FCSTD DOCUMENT  (FreeCAD 0.21RUnknown)
Label: pcb wise
License: All rights reserved
LicenseURL: https://en.wikipedia.org/wiki/All_rights_reserved
objects: Part::FeaturePython×2, Part::Cylinder×2, Part::Cut×2, Part::Feature×1
note: 7 computed .brp shape members not serialized (recipe doc carries the construction recipe); baked Part::Feature solids carry a one-line shape summary decoded from their .brp

FEATURE [Part::Feature] Part__Feature  label="Vise_Sliding_Jaw"
  shape: large baked B-rep (55 MB .brp); summary skipped
FEATURE [Part::FeaturePython] Tube  label="Tube 1"  # WARN: FeaturePython — macro-defined, semantics opaque (R4)
  AttacherType = Attacher::AttachEngine3D
  Height = 96
  InnerRadius = 1.65
  OuterRadius = 4
  Placement = pos=(15,25,-89.85) rot=(0,0,1;0rad)
FEATURE [Part::FeaturePython] Tube001  label="Tube 2"  # WARN: FeaturePython — macro-defined, semantics opaque (R4)
  AttacherType = Attacher::AttachEngine3D
  Height = 96
  InnerRadius = 1.65
  OuterRadius = 4
  Placement = pos=(15,-25,-89.85) rot=(0,0,1;0rad)
FEATURE [Part::Cylinder] Cylinder  label="Cylinder 1"
  Angle = 360
  AttacherType = Attacher::AttachEngine3D
  FirstAngle = 0
  Height = 7
  Placement = pos=(15,-25,-96.8) rot=(0,0,1;0rad)
  Radius = 4.5
  SecondAngle = 0
FEATURE [Part::Cylinder] Cylinder001  label="Cylinder 2"
  Angle = 360
  AttacherType = Attacher::AttachEngine3D
  FirstAngle = 0
  Height = 7
  Placement = pos=(15,25,-96.8) rot=(0,0,1;0rad)
  Radius = 4.5
  SecondAngle = 0
FEATURE [Part::Cut] Cut
  Base = -> Part__Feature
  Tool = -> Cylinder
FEATURE [Part::Cut] Cut001
  Base = -> Cut
  Tool = -> Cylinder001
